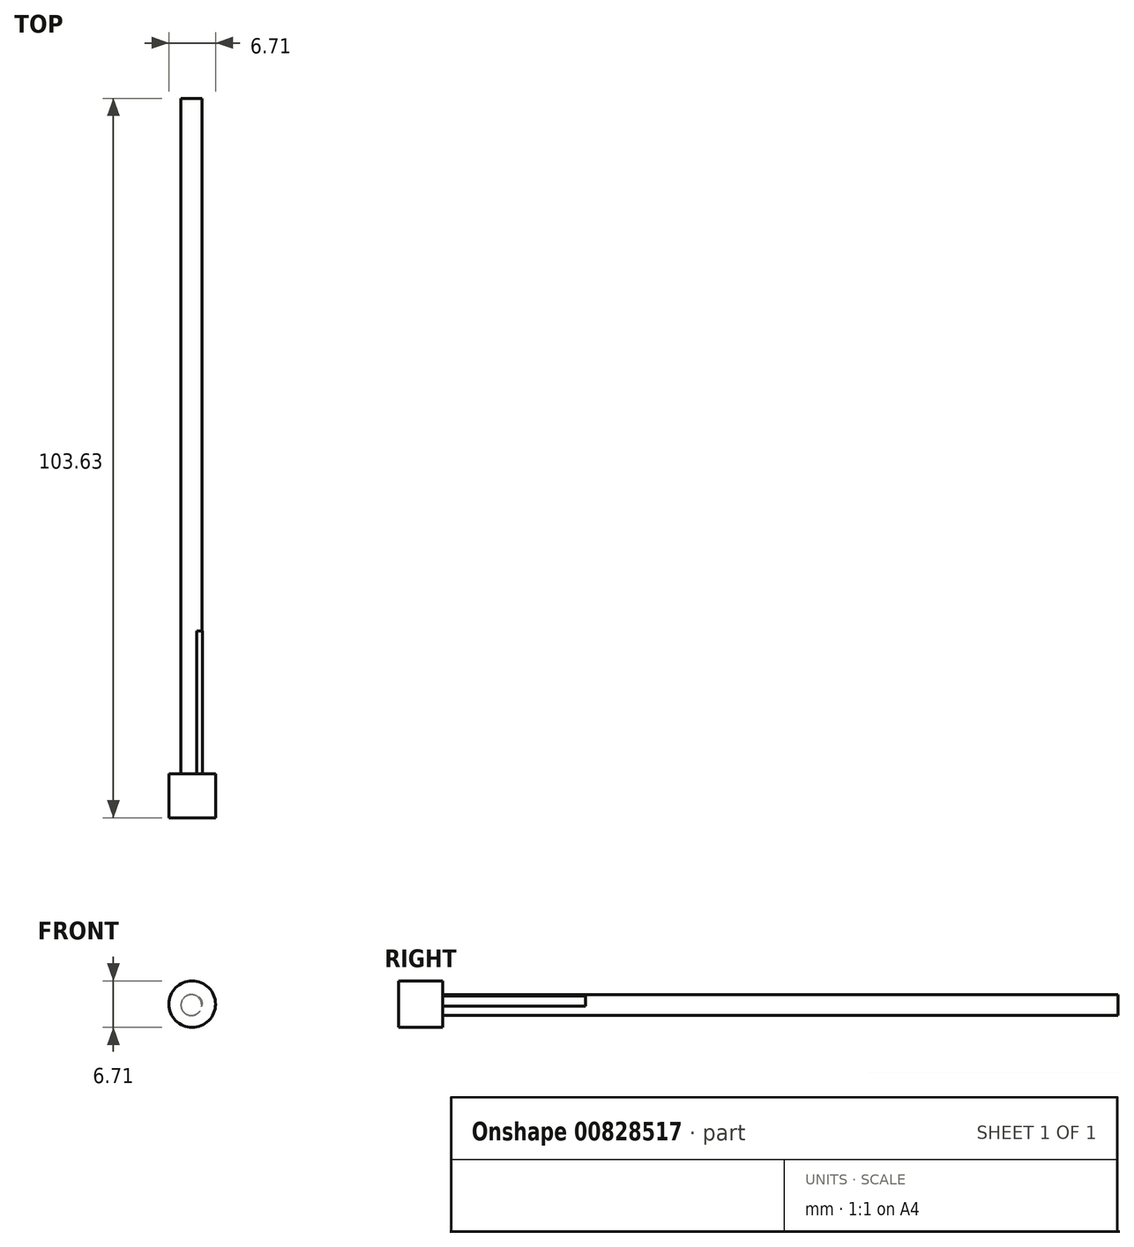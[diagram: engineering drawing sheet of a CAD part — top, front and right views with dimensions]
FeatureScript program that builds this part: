
annotation { "Feature Type Name" : "Feature", "Feature Type Description" : "" }
export const myFeature = defineFeature(function(context is Context, id is Id, definition is map)
    precondition{}
    {
        {
            var Q0;
            Q0=qCreatedBy(makeId("Front.planeOp"),FACE);
            var sketch = newSketch(context, id + "F0", { "sketchPlane" : qUnion([Q0])});
            skCircle(sketch, "E0", {"center": v(-35.7, 10.55) * mm, "radius": 3.35 * mm});
            skSolve(sketch);
        }
        {
            var Q0;
            Q0 = qSketchRegion(id + "F0", true);
            extrude(context, id + "F1", {"entities" : qUnion([Q0]), "depth" : 6.35 * mm, "offsetDistance" : 25.4 * mm});
        }
        {
            var Q0;
            Q0=qCreatedBy(makeId("Front.planeOp"),FACE);
            var sketch = newSketch(context, id + "F2", { "sketchPlane" : qUnion([Q0])});
            skCircle(sketch, "E1", {"center": v(-35.8, 10.43) * mm, "radius": 1.5 * mm});
            skSolve(sketch);
        }
        {
            var Q0;
            Q0 = qSketchRegion(id + "F2", true);
            extrude(context, id + "F3", {"entities" : qUnion([Q0]), "operationType" : NewBodyOperationType.ADD, "oppositeDirection" : true, "depth" : 97.28 * mm, "offsetDistance" : 25.4 * mm});
        }
        {
            var Q0;
            Q0=qCreatedBy(makeId("Front.planeOp"),FACE);
            var sketch = newSketch(context, id + "F4", { "sketchPlane" : qUnion([Q0])});
            skCircle(sketch, "E2", {"center": v(-35.33, 10.67) * mm, "radius": 1.08 * mm});
            skSolve(sketch);
        }
        {
            var Q0;
            Q0 = qSketchRegion(id + "F4", true);
            extrude(context, id + "F5", {"entities" : qUnion([Q0]), "operationType" : NewBodyOperationType.ADD, "oppositeDirection" : true, "depth" : 20.57 * mm, "offsetDistance" : 25.4 * mm});
        }
    });
